# Revit family: Reece_Vanity_Kado_Arc_Drawer
name_source: partatom
category: Casework
revit_build: Autodesk Revit 2018 (Build: 20180329_1100(x64)
units: mm (PartAtom-declared; Revit-internal decimal feet)

## family parameters
Always vertical = Yes
Cut with Voids When Loaded = Yes
Room Calculation Point = Yes
Shared = Yes
Work Plane-Based = Yes

## types (1)
- Reece_All_Types
    Default Elevation = 0 mm  [stored 0 ft]
    Depth = 460 mm  [stored 1.50919 ft]
    Disclaimer = THIS FILE IS THE PROPERTY OF THE REECE GROUP. IT MAY NOT BE REPRODUCED, REVERSE-ENGINEERED, OR MODIFIED. ANY REPUBLICATION, TRANSMISSION, OR DISTRIBUTION FOR THE PURPOSE OF COMMERCIALLY EXPLOITING THE FILES IS PROHIBITED.
    Finish = Please refer to Colour, Finish and Material Variations Document for more information.
    Height = 502 mm  [stored 1.64698 ft]
    Reece_Basin_Outlet = 40 mm  [stored 0.131234 ft]
    Reece_Cabinet_Height Dimension = 490 mm  [stored 1.60761 ft]
    Reece_Centre_Panel_2 = No
    Reece_Detail_Additional = Please refer to Colour, Finish and Material Variations Document for more information.
    Reece_Detail_Disclaimer = THIS FILE IS THE PROPERTY OF THE REECE GROUP. IT MAY NOT BE REPRODUCED, REVERSE-ENGINEERED, OR MODIFIED. ANY REPUBLICATION, TRANSMISSION, OR DISTRIBUTION FOR THE PURPOSE OF COMMERCIALLY EXPLOITING THE FILES IS PROHIBITED.
    Reece_Drawer_Back Panel_Height = 0 mm  [stored 0 ft]
    Reece_Material_Benchtop = Reece_Corian_Solid_Surface_Glacier White
    Reece_Material_Cabinet = Reece_Timber_Australian Chestnut
    Reece_Material_Secondary = Reece_Timber_Australian Chestnut
    Reece_Overall_Capacity = 0 L
    Reece_Panel_Thickness_Top = 12 mm  [stored 0.0393701 ft]
    Reece_Product_Brand = Kado
    Reece_Product_Mount = Wall Mounted
    Reece_Product_Sub Brand = Arc
    Reece_Product_Type = Vanity
    Reece_Product_Web Page = https://www.reece.com.au
    Reece_Vanity_Bowl_Count = 1
    Reece_Vanity_Top_Depth = 460 mm  [stored 1.50919 ft]
    Reece_Vanity_Top_Width = 900 mm  [stored 2.95276 ft]
    Reece_Vertical_Division_Count = 1
    Width = 900 mm  [stored 2.95276 ft]

note: [stored X ft] marks values corroborated as IEEE doubles in the binary element streams (Revit-internal decimal feet)

## geometry (parser evidence)
native form markers: Sweep x5
no freeform markers — native parametric forms only
